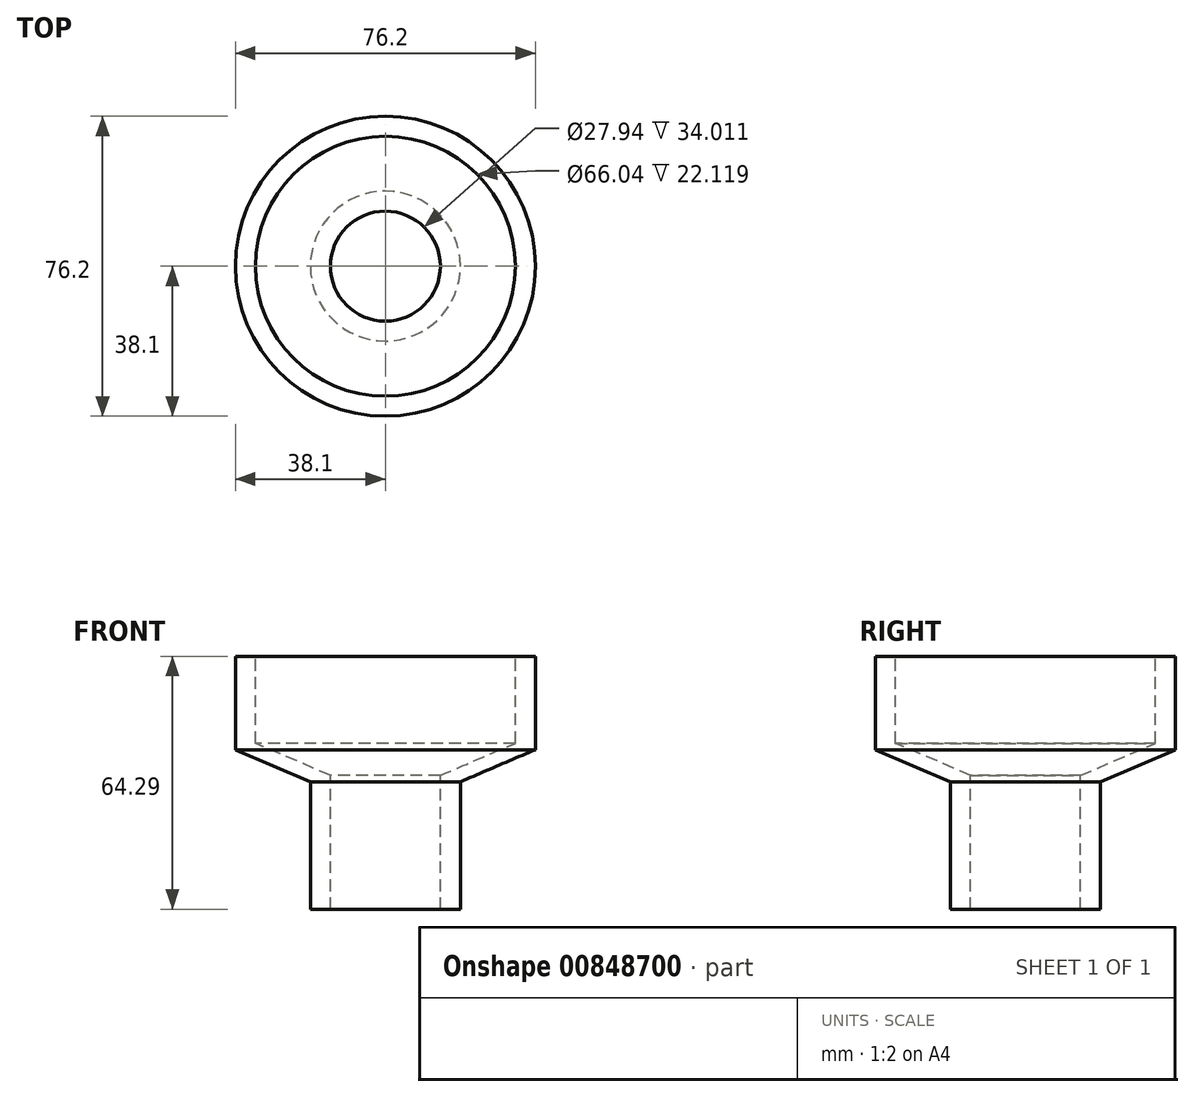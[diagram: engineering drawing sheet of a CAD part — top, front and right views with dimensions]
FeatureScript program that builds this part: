
annotation { "Feature Type Name" : "Feature", "Feature Type Description" : "" }
export const myFeature = defineFeature(function(context is Context, id is Id, definition is map)
    precondition{}
    {
        {
            var Q0;
            Q0=qCreatedBy(makeId("Front.planeOp"),FACE);
            var sketch = newSketch(context, id + "F0", { "sketchPlane" : qUnion([Q0])});
            skLineSegment(sketch, "E0", {"start": v(-19.05, -1.63) * mm, "end": v(-19.05, -34.01) * mm});
            skLineSegment(sketch, "E1", {"start": v(-19.05, -34.01) * mm, "end": v(-13.97, -34.01) * mm});
            skLineSegment(sketch, "E2", {"start": v(-13.97, -34.01) * mm, "end": v(-13.97, 0) * mm});
            skLineSegment(sketch, "E3", {"start": v(-13.97, 0) * mm, "end": v(-33.02, 8.16) * mm});
            skLineSegment(sketch, "E4", {"start": v(-38.1, 6.54) * mm, "end": v(-19.05, -1.63) * mm});
            skLineSegment(sketch, "E5", {"start": v(-38.1, 6.54) * mm, "end": v(-38.1, 30.28) * mm});
            skLineSegment(sketch, "E6", {"start": v(-38.1, 30.28) * mm, "end": v(-33.02, 30.28) * mm});
            skLineSegment(sketch, "E7", {"start": v(-33.02, 30.28) * mm, "end": v(-33.02, 8.16) * mm});
            skLineSegment(sketch, "E8", {"start": v(-38.1, 6.54) * mm, "end": v(-33.02, 8.16) * mm});
            skLineSegment(sketch, "E9", {"start": v(-19.05, -1.63) * mm, "end": v(-13.97, 0) * mm});
            skLineSegment(sketch, "E10", {"start": v(0, 51.92) * mm, "end": v(0, -40.5) * mm});
            skSolve(sketch);
        }
        {
            var Q0;
            Q0=makeQuery(id+"F0.imprint","IMPRINT",FACE,{"disambiguationData":[TD([[makeQuery(id+"F0.imprint","IMPRINT",EDGE,{"derivedFrom":sQuery(id+"F0.wireOp",EDGE,"E5")}),-1.0]])]});
            var Q1;
            Q1=makeQuery(id+"F0.imprint","IMPRINT",FACE,{"disambiguationData":[TD([[makeQuery(id+"F0.imprint","IMPRINT",EDGE,{"derivedFrom":sQuery(id+"F0.wireOp",EDGE,"E3")}),1.0]])]});
            var Q2;
            Q2=makeQuery(id+"F0.imprint","IMPRINT",FACE,{"disambiguationData":[TD([[makeQuery(id+"F0.imprint","IMPRINT",EDGE,{"derivedFrom":sQuery(id+"F0.wireOp",EDGE,"E0")}),1.0]])]});
            var Q3;
            Q3=sQuery(id+"F0.wireOp",EDGE,"E10");
            revolve(context, id + "F1", {"surfaceOperationType" : NewSurfaceOperationType.NEW, "entities" : qUnion([Q0, Q1, Q2]), "axis" : qUnion([Q3]), "revolveType" : RevolveType.FULL});
        }
    });
